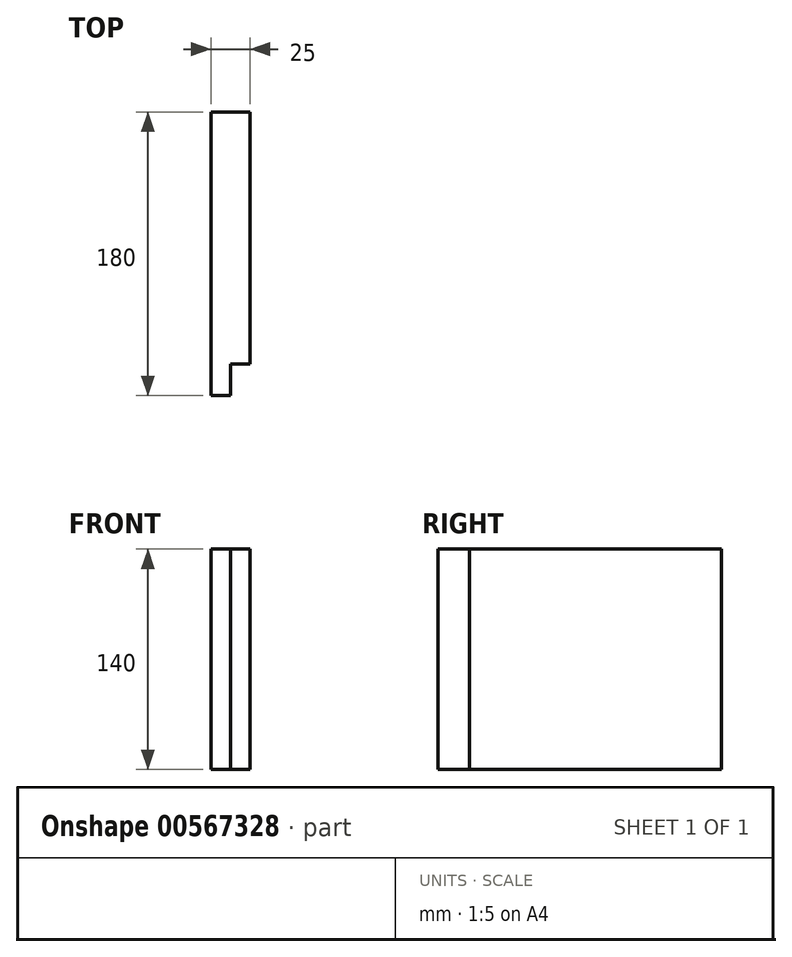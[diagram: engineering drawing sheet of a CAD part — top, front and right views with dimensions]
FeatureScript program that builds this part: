
annotation { "Feature Type Name" : "Feature", "Feature Type Description" : "" }
export const myFeature = defineFeature(function(context is Context, id is Id, definition is map)
    precondition{}
    {
        {
            var Q0;
            Q0=qCreatedBy(makeId("Right.planeOp"),FACE);
            var sketch = newSketch(context, id + "F0", { "sketchPlane" : qUnion([Q0])});
            skLineSegment(sketch, "E0.bottom", {"start": v(0, 0) * mm, "end": v(180, 0) * mm});
            skLineSegment(sketch, "E0.top", {"start": v(20, 140) * mm, "end": v(180, 140) * mm});
            skLineSegment(sketch, "E0.left", {"start": v(0, 0) * mm, "end": v(0, 35) * mm});
            skLineSegment(sketch, "E0.right", {"start": v(180, 0) * mm, "end": v(180, 140) * mm});
            skPoint(sketch, "E1.orphan", {"position": v(0, 140) * mm});
            skLineSegment(sketch, "E2.trimOffspring", {"start": v(0, 70) * mm, "end": v(0, 105) * mm});
            skPoint(sketch, "E3.orphan", {"position": v(20, 0) * mm});
            skLineSegment(sketch, "E4", {"start": v(0, 35) * mm, "end": v(0, 140) * mm});
            skLineSegment(sketch, "E5", {"start": v(0, 140) * mm, "end": v(20, 140) * mm});
            skPoint(sketch, "E6.end.orphan", {"position": v(20, 70) * mm});
            skSolve(sketch);
        }
        {
            var Q0;
            Q0=makeQuery(id+"F0.imprint","IMPRINT",FACE,{"disambiguationData":[TD([[makeQuery(id+"F0.imprint","IMPRINT",EDGE,{"derivedFrom":sQuery(id+"F0.wireOp",EDGE,"E0.bottom")}),1.0]])]});
            extrude(context, id + "F1", {"entities" : qUnion([Q0]), "depth" : 25 * mm, "offsetDistance" : 25 * mm});
        }
        {
            var Q0;
            Q0=makeQuery(id+"F1.opExtrude","SWEPT_FACE",FACE,{"disambiguationData":[OSD([sQuery(id+"F0.wireOp",EDGE,"E0.left"),sQuery(id+"F0.wireOp",EDGE,"E4")])]});
            var sketch = newSketch(context, id + "F2", { "sketchPlane" : qUnion([Q0])});
            skLineSegment(sketch, "E7", {"start": v(12.5, 140) * mm, "end": v(12.5, 0) * mm});
            skLineSegment(sketch, "E8", {"start": v(12.5, 0) * mm, "end": v(25, 0) * mm});
            skLineSegment(sketch, "E9", {"start": v(12.5, 140) * mm, "end": v(25, 140) * mm});
            skLineSegment(sketch, "E10", {"start": v(25, 140) * mm, "end": v(25, 0) * mm});
            skSolve(sketch);
        }
        {
            var Q0;
            Q0=makeQuery(id+"F2.imprint","IMPRINT",FACE,{"disambiguationData":[TD([[makeQuery(id+"F2.imprint","IMPRINT",EDGE,{"derivedFrom":sQuery(id+"F2.wireOp",EDGE,"E7")}),1.0]])]});
            extrude(context, id + "F3", {"entities" : qUnion([Q0]), "operationType" : NewBodyOperationType.REMOVE, "oppositeDirection" : true, "depth" : 20 * mm, "offsetDistance" : 25 * mm});
        }
    });
